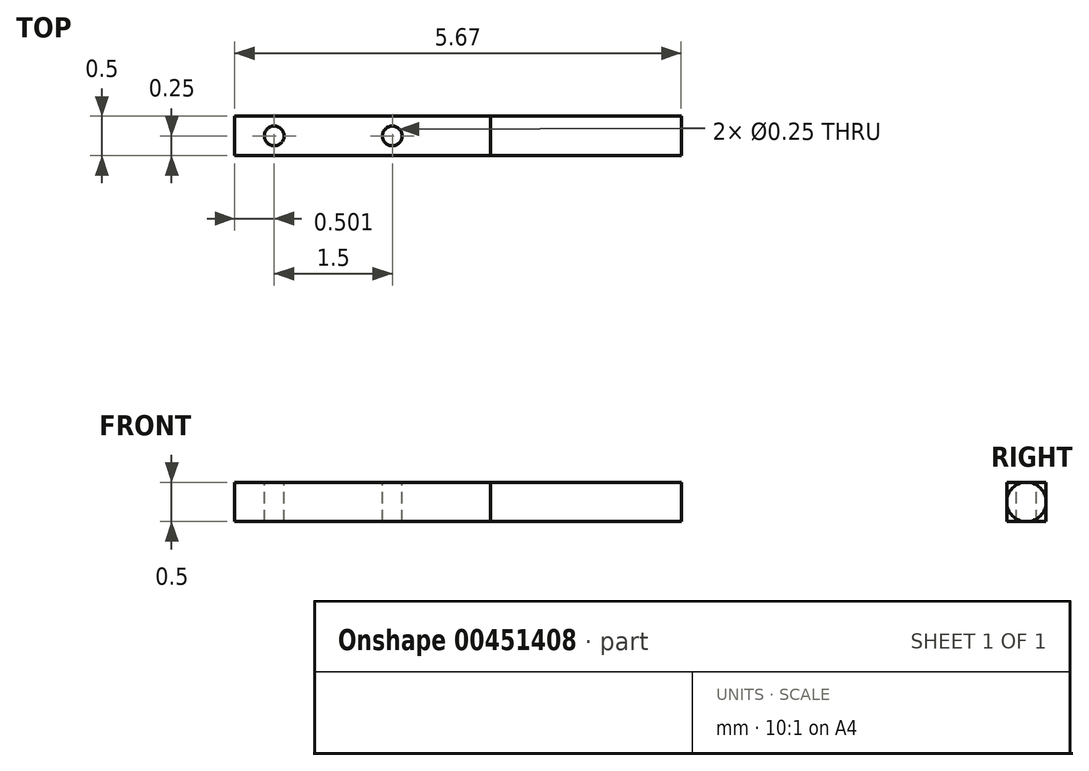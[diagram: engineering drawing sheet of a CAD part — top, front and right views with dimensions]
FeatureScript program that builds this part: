
annotation { "Feature Type Name" : "Feature", "Feature Type Description" : "" }
export const myFeature = defineFeature(function(context is Context, id is Id, definition is map)
    precondition{}
    {
        {
            var Q0;
            Q0=qCreatedBy(makeId("Front.planeOp"),FACE);
            var sketch = newSketch(context, id + "F0", { "sketchPlane" : qUnion([Q0])});
            skLineSegment(sketch, "E0.bottom", {"start": v(0, 0.25) * mm, "end": v(-3.25, 0.25) * mm});
            skLineSegment(sketch, "E0.top", {"start": v(0, -0.25) * mm, "end": v(-3.25, -0.25) * mm});
            skLineSegment(sketch, "E0.left", {"start": v(0, 0.25) * mm, "end": v(0, -0.25) * mm});
            skLineSegment(sketch, "E0.right", {"start": v(-3.25, 0.25) * mm, "end": v(-3.25, -0.25) * mm});
            skLineSegment(sketch, "E1.bottom", {"start": v(0, 0) * mm, "end": v(2.42, 0) * mm});
            skLineSegment(sketch, "E1.top", {"start": v(0, 0.25) * mm, "end": v(2.42, 0.25) * mm});
            skLineSegment(sketch, "E1.left", {"start": v(0, 0) * mm, "end": v(0, 0.25) * mm});
            skLineSegment(sketch, "E1.right", {"start": v(2.42, 0) * mm, "end": v(2.42, 0.25) * mm});
            skSolve(sketch);
        }
        {
            var Q0;
            Q0=makeQuery(id+"F0.imprint","IMPRINT",FACE,{"disambiguationData":[TD([[makeQuery(id+"F0.imprint","IMPRINT",EDGE,{"derivedFrom":sQuery(id+"F0.wireOp",EDGE,"E0.bottom")}),1.0]])]});
            extrude(context, id + "F1", {"entities" : qUnion([Q0]), "endBound" : BoundingType.SYMMETRIC, "depth" : 0.5 * mm});
        }
        {
            var Q0;
            Q0=makeQuery(id+"F0.imprint","IMPRINT",FACE,{"disambiguationData":[TD([[makeQuery(id+"F0.imprint","IMPRINT",EDGE,{"derivedFrom":sQuery(id+"F0.wireOp",EDGE,"E1.bottom")}),1.0]])]});
            var Q1;
            Q1=sQuery(id+"F0.wireOp",EDGE,"E1.bottom");
            revolve(context, id + "F2", {"operationType" : NewBodyOperationType.ADD, "entities" : qUnion([Q0]), "axis" : qUnion([Q1]), "revolveType" : RevolveType.FULL});
        }
        {
            var Q0;
            Q0=makeQuery(id+"F1.opExtrude","SWEPT_FACE",FACE,{"disambiguationData":[OSD([sQuery(id+"F0.wireOp",EDGE,"E0.bottom")])]});
            var sketch = newSketch(context, id + "F3", { "sketchPlane" : qUnion([Q0])});
            skCircle(sketch, "E2", {"center": v(-2.75, 0) * mm, "radius": 0.12 * mm});
            skCircle(sketch, "E3", {"center": v(-1.25, 0) * mm, "radius": 0.12 * mm});
            skSolve(sketch);
        }
        {
            var Q0;
            Q0=qSketchRegion(id+"F3",true);
            extrude(context, id + "F4", {"entities" : qUnion([Q0]), "operationType" : NewBodyOperationType.REMOVE, "endBound" : BoundingType.THROUGH_ALL, "oppositeDirection" : true, "depth" : 25 * mm});
        }
    });
